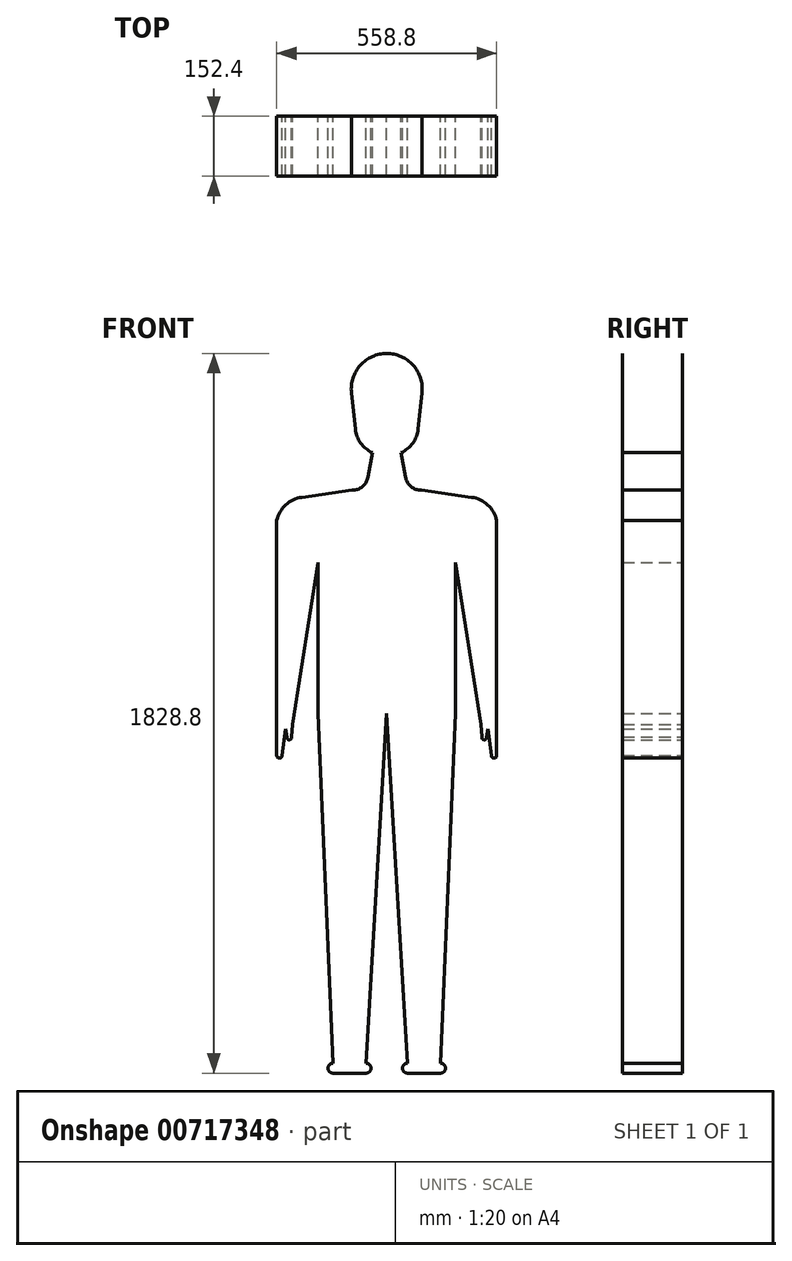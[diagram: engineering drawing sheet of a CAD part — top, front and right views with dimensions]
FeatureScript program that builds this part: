
annotation { "Feature Type Name" : "Feature", "Feature Type Description" : "" }
export const myFeature = defineFeature(function(context is Context, id is Id, definition is map)
    precondition{}
    {
        {
            var Q0;
            Q0=qCreatedBy(makeId("Front.planeOp"),FACE);
            var sketch = newSketch(context, id + "F0", { "sketchPlane" : qUnion([Q0])});
            skLineSegment(sketch, "E0.bottom", {"start": v(-279.4, 914.4) * mm, "end": v(279.4, 914.4) * mm, "construction": true});
            skLineSegment(sketch, "E0.top", {"start": v(-279.4, -914.4) * mm, "end": v(279.4, -914.4) * mm, "construction": true});
            skLineSegment(sketch, "E0.left", {"start": v(-279.4, 914.4) * mm, "end": v(-279.4, -914.4) * mm, "construction": true});
            skLineSegment(sketch, "E0.right", {"start": v(279.4, 914.4) * mm, "end": v(279.4, -914.4) * mm, "construction": true});
            skLineSegment(sketch, "E1", {"start": v(0, 914.4) * mm, "end": v(0, -914.4) * mm, "construction": true});
            skArc(sketch, "E2", {"start": v(89.61, 814.32) * mm, "mid": v(66.8, 884.54) * mm, "end": v(-0.72, 914.4) * mm});
            skLineSegment(sketch, "E3", {"start": v(89.61, 814.32) * mm, "end": v(79.8, 722.3) * mm});
            skArc(sketch, "E4", {"start": v(36.77, 662.17) * mm, "mid": v(66.2, 686.57) * mm, "end": v(79.8, 722.3) * mm});
            skLineSegment(sketch, "E5", {"start": v(36.77, 662.17) * mm, "end": v(47.62, 599.88) * mm});
            skArc(sketch, "E6", {"start": v(47.62, 599.88) * mm, "mid": v(61.7, 575.83) * mm, "end": v(88.11, 566.89) * mm});
            skLineSegment(sketch, "E7", {"start": v(88.11, 566.89) * mm, "end": v(215.58, 548.9) * mm});
            skArc(sketch, "E8", {"start": v(279.4, 490.41) * mm, "mid": v(256.56, 529.55) * mm, "end": v(215.58, 548.9) * mm});
            skLineSegment(sketch, "E9", {"start": v(0, 0) * mm, "end": v(52.74, -888.88) * mm});
            skArc(sketch, "E10", {"start": v(136.5, -914.4) * mm, "mid": v(149.26, -901.64) * mm, "end": v(136.5, -888.88) * mm});
            skArc(sketch, "E11", {"start": v(52.74, -888.88) * mm, "mid": v(39.97, -901.64) * mm, "end": v(52.74, -914.4) * mm});
            skLineSegment(sketch, "E12", {"start": v(52.74, -914.4) * mm, "end": v(136.5, -914.4) * mm});
            skLineSegment(sketch, "E13", {"start": v(136.5, -888.88) * mm, "end": v(174.92, 0) * mm});
            skLineSegment(sketch, "E14", {"start": v(279.4, 490.41) * mm, "end": v(279.4, -107.24) * mm});
            skArc(sketch, "E15", {"start": v(265.85, -107.24) * mm, "mid": v(272.63, -114.02) * mm, "end": v(279.4, -107.24) * mm});
            skLineSegment(sketch, "E16", {"start": v(265.85, -107.24) * mm, "end": v(256.67, -39.25) * mm});
            skLineSegment(sketch, "E17", {"start": v(256.67, -39.25) * mm, "end": v(253.89, -61.76) * mm});
            skArc(sketch, "E18", {"start": v(241.41, -60.68) * mm, "mid": v(247.13, -67.23) * mm, "end": v(253.89, -61.76) * mm});
            skLineSegment(sketch, "E19", {"start": v(241.41, -60.68) * mm, "end": v(239.8, -28.75) * mm});
            skLineSegment(sketch, "E20", {"start": v(174.92, 0) * mm, "end": v(174.92, 383.5) * mm});
            skLineSegment(sketch, "E21", {"start": v(174.92, 383.5) * mm, "end": v(239.8, -28.75) * mm});
            skArc(sketch, "E22.MirrorCS", {"start": v(-89.61, 814.32) * mm, "mid": v(-66.8, 884.54) * mm, "end": v(0.72, 914.4) * mm});
            skLineSegment(sketch, "E23.MirrorCS", {"start": v(-89.61, 814.32) * mm, "end": v(-79.8, 722.3) * mm});
            skArc(sketch, "E24.MirrorCS", {"start": v(-36.77, 662.17) * mm, "mid": v(-66.2, 686.57) * mm, "end": v(-79.8, 722.3) * mm});
            skLineSegment(sketch, "E25.MirrorCS", {"start": v(-36.77, 662.17) * mm, "end": v(-47.62, 599.88) * mm});
            skArc(sketch, "E26.MirrorCS", {"start": v(-47.62, 599.88) * mm, "mid": v(-61.7, 575.83) * mm, "end": v(-88.11, 566.89) * mm});
            skLineSegment(sketch, "E27.MirrorCS", {"start": v(-88.11, 566.89) * mm, "end": v(-215.58, 548.9) * mm});
            skArc(sketch, "E28.MirrorCS", {"start": v(-279.4, 490.41) * mm, "mid": v(-256.56, 529.55) * mm, "end": v(-215.58, 548.9) * mm});
            skLineSegment(sketch, "E29.MirrorCS", {"start": v(-279.4, 490.41) * mm, "end": v(-279.4, -107.24) * mm});
            skArc(sketch, "E30.MirrorCS", {"start": v(-265.85, -107.24) * mm, "mid": v(-272.63, -114.02) * mm, "end": v(-279.4, -107.24) * mm});
            skLineSegment(sketch, "E31.MirrorCS", {"start": v(-265.85, -107.24) * mm, "end": v(-256.67, -39.25) * mm});
            skLineSegment(sketch, "E32.MirrorCS", {"start": v(-256.67, -39.25) * mm, "end": v(-253.89, -61.76) * mm});
            skArc(sketch, "E33.MirrorCS", {"start": v(-241.41, -60.68) * mm, "mid": v(-247.13, -67.23) * mm, "end": v(-253.89, -61.76) * mm});
            skLineSegment(sketch, "E34.MirrorCS", {"start": v(-241.41, -60.68) * mm, "end": v(-239.8, -28.75) * mm});
            skLineSegment(sketch, "E35.MirrorCS", {"start": v(-174.92, 383.5) * mm, "end": v(-239.8, -28.75) * mm});
            skLineSegment(sketch, "E36.MirrorCS", {"start": v(-174.92, 0) * mm, "end": v(-174.92, 383.5) * mm});
            skLineSegment(sketch, "E37.MirrorCS", {"start": v(-136.5, -888.88) * mm, "end": v(-174.92, 0) * mm});
            skLineSegment(sketch, "E38.MirrorCS", {"start": v(0, 0) * mm, "end": v(-52.74, -888.88) * mm});
            skArc(sketch, "E39.MirrorCS", {"start": v(-52.74, -888.88) * mm, "mid": v(-39.97, -901.64) * mm, "end": v(-52.74, -914.4) * mm});
            skArc(sketch, "E40.MirrorCS", {"start": v(-136.5, -914.4) * mm, "mid": v(-149.26, -901.64) * mm, "end": v(-136.5, -888.88) * mm});
            skLineSegment(sketch, "E41.MirrorCS", {"start": v(-52.74, -914.4) * mm, "end": v(-136.5, -914.4) * mm});
            skSolve(sketch);
        }
        {
            var Q0;
            Q0 = qSketchRegion(id + "F0", true);
            extrude(context, id + "F1", {"entities" : qUnion([Q0]), "endBound" : BoundingType.SYMMETRIC, "depth" : 152.4 * mm, "offsetDistance" : 25.4 * mm});
        }
    });
